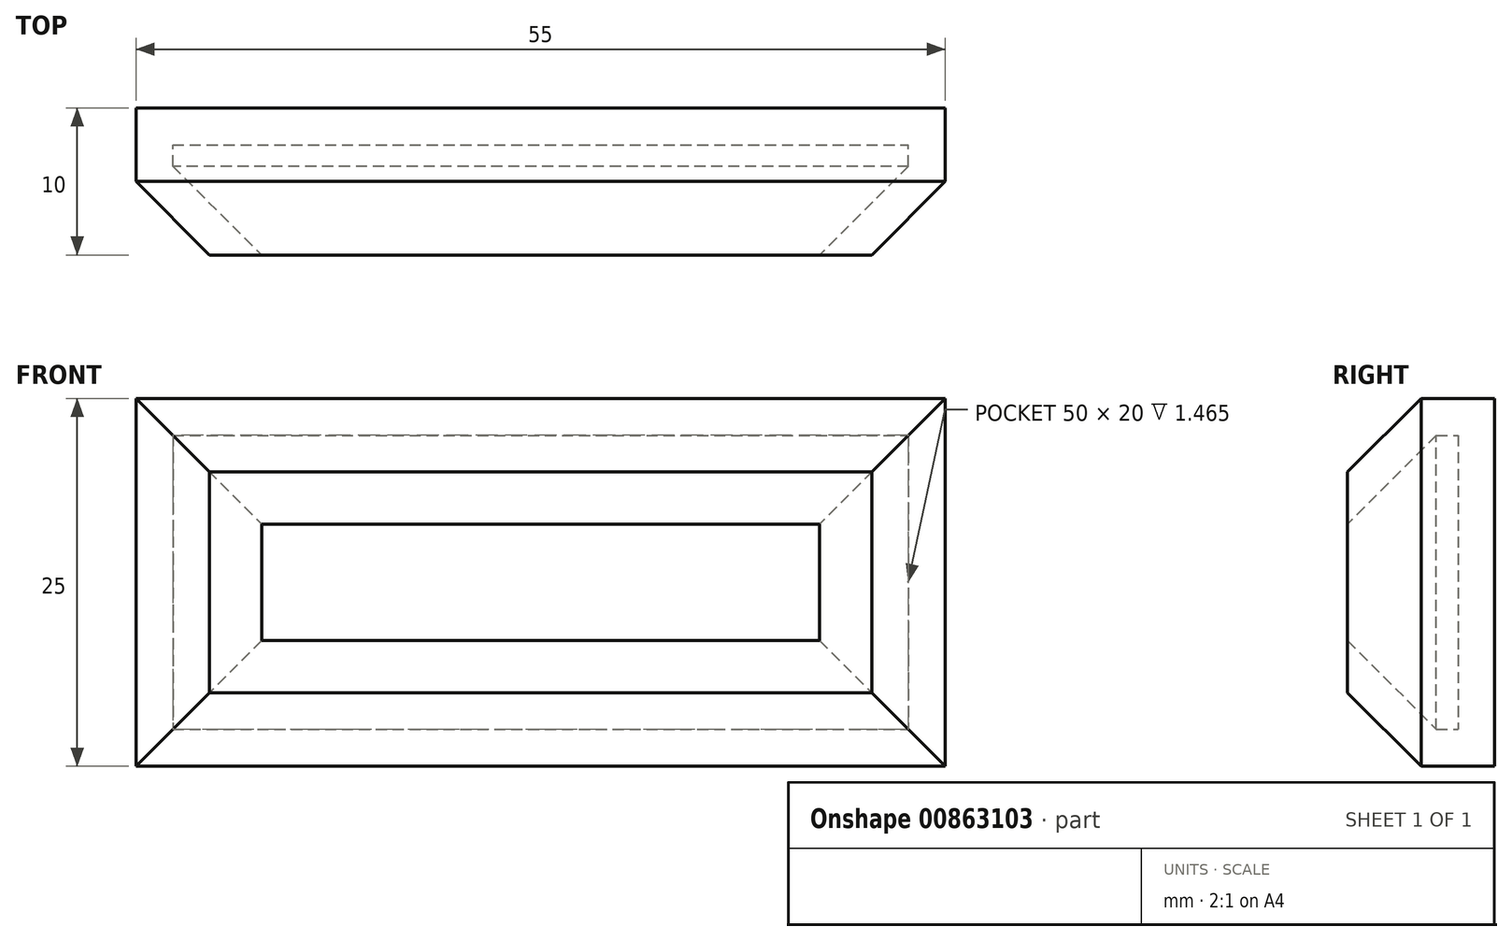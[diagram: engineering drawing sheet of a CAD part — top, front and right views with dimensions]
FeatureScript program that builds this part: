
annotation { "Feature Type Name" : "Feature", "Feature Type Description" : "" }
export const myFeature = defineFeature(function(context is Context, id is Id, definition is map)
    precondition{}
    {
        {
            var Q0;
            Q0=qCreatedBy(makeId("Front.planeOp"),FACE);
            var sketch = newSketch(context, id + "F0", { "sketchPlane" : qUnion([Q0])});
            skLineSegment(sketch, "E0.bottom", {"start": v(-38.03, 30.35) * mm, "end": v(16.97, 30.35) * mm});
            skLineSegment(sketch, "E0.top", {"start": v(-38.03, 5.35) * mm, "end": v(16.97, 5.35) * mm});
            skLineSegment(sketch, "E0.left", {"start": v(-38.03, 30.35) * mm, "end": v(-38.03, 5.35) * mm});
            skLineSegment(sketch, "E0.right", {"start": v(16.97, 30.35) * mm, "end": v(16.97, 5.35) * mm});
            skSolve(sketch);
        }
        {
            var Q0;
            Q0=makeQuery(id+"F0.imprint","IMPRINT",FACE,{"disambiguationData":[TD([[makeQuery(id+"F0.imprint","IMPRINT",EDGE,{"derivedFrom":sQuery(id+"F0.wireOp",EDGE,"E0.bottom")}),-1.0]])]});
            extrude(context, id + "F1", {"entities" : qUnion([Q0]), "depth" : 10 * mm, "offsetDistance" : 25 * mm});
        }
        {
            var Q0;
            Q0=makeQuery(id+"F1.opExtrude","CAP_FACE",FACE,{"disambiguationData":[OSD([sQuery(id+"F0.wireOp",EDGE,"E0.bottom"),sQuery(id+"F0.wireOp",EDGE,"E0.top"),sQuery(id+"F0.wireOp",EDGE,"E0.left"),sQuery(id+"F0.wireOp",EDGE,"E0.right")])],"isStart":false});
            chamfer(context, id + "F2", {"entities" : qUnion([Q0]), "width" : 5 * mm, "tangentPropagation" : true});
        }
        {
            var Q0;
            Q0=makeQuery(id+"F1.opExtrude","CAP_FACE",FACE,{"disambiguationData":[OSD([sQuery(id+"F0.wireOp",EDGE,"E0.bottom"),sQuery(id+"F0.wireOp",EDGE,"E0.top"),sQuery(id+"F0.wireOp",EDGE,"E0.left"),sQuery(id+"F0.wireOp",EDGE,"E0.right")])],"isStart":false});
            shell(context, id + "F3", {"entities" : qUnion([Q0]), "thickness" : 2.5 * mm});
        }
    });
